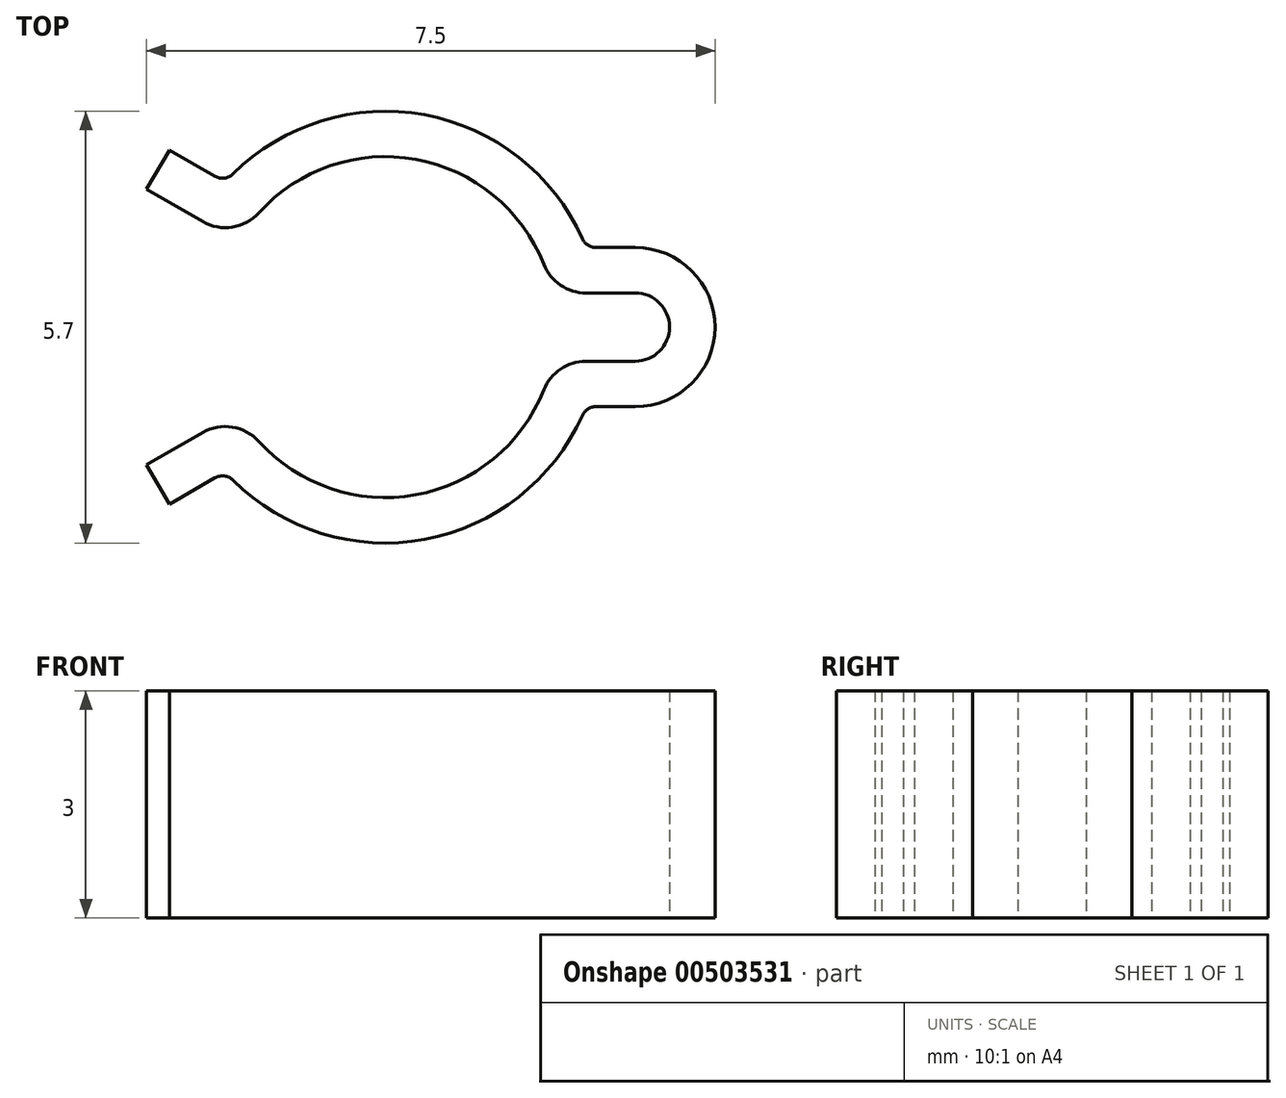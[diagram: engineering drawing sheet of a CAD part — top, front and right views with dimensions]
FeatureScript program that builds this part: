
annotation { "Feature Type Name" : "Feature", "Feature Type Description" : "" }
export const myFeature = defineFeature(function(context is Context, id is Id, definition is map)
    precondition{}
    {
        {
            var Q0;
            Q0=qCreatedBy(makeId("Top.planeOp"),FACE);
            var sketch = newSketch(context, id + "F0", { "sketchPlane" : qUnion([Q0])});
            skArc(sketch, "E0", {"start": v(0.7, 0.28) * mm, "mid": v(0.13, 0.74) * mm, "end": v(-0.56, 0.5) * mm});
            skArc(sketch, "E1", {"start": v(0.8, 0.31) * mm, "mid": v(0.15, 0.84) * mm, "end": v(-0.63, 0.57) * mm});
            skLineSegment(sketch, "E2", {"start": v(0, 0) * mm, "end": v(-1.2, 0.7) * mm, "construction": true});
            skLineSegment(sketch, "E3", {"start": v(0, 0) * mm, "end": v(-1.2, -0.7) * mm, "construction": true});
            skCircle(sketch, "E4", {"center": v(0, 0) * mm, "radius": 1.35 * mm, "construction": true});
            skArc(sketch, "E5", {"start": v(1.1, -0.25) * mm, "mid": v(1.35, 0) * mm, "end": v(1.1, 0.25) * mm});
            skArc(sketch, "E6", {"start": v(1.1, -0.15) * mm, "mid": v(1.25, 0) * mm, "end": v(1.1, 0.15) * mm});
            skLineSegment(sketch, "E7", {"start": v(1.1, 0.25) * mm, "end": v(0.88, 0.25) * mm});
            skLineSegment(sketch, "E8", {"start": v(1.1, 0.15) * mm, "end": v(0.88, 0.15) * mm});
            skLineSegment(sketch, "E9", {"start": v(1.1, -0.15) * mm, "end": v(0.88, -0.15) * mm});
            skLineSegment(sketch, "E10", {"start": v(1.1, -0.25) * mm, "end": v(0.88, -0.25) * mm});
            skPoint(sketch, "E11.visualSharp", {"position": v(0.81, 0.25) * mm});
            skArc(sketch, "E11.filletArc", {"start": v(0.8, 0.31) * mm, "mid": v(0.83, 0.27) * mm, "end": v(0.88, 0.25) * mm});
            skPoint(sketch, "E12.visualSharp", {"position": v(0.73, 0.15) * mm});
            skArc(sketch, "E12.filletArc", {"start": v(0.7, 0.28) * mm, "mid": v(0.77, 0.18) * mm, "end": v(0.88, 0.15) * mm});
            skPoint(sketch, "E13.visualSharp", {"position": v(0.81, -0.25) * mm});
            skArc(sketch, "E13.filletArc", {"start": v(0.88, -0.25) * mm, "mid": v(0.83, -0.27) * mm, "end": v(0.8, -0.31) * mm});
            skPoint(sketch, "E14.visualSharp", {"position": v(0.73, -0.15) * mm});
            skArc(sketch, "E14.filletArc", {"start": v(0.88, -0.15) * mm, "mid": v(0.77, -0.18) * mm, "end": v(0.7, -0.28) * mm});
            skLineSegment(sketch, "E15", {"start": v(1.35, 0) * mm, "end": v(-1.05, 0) * mm, "construction": true});
            skLineSegment(sketch, "E16", {"start": v(-1.05, -0.6) * mm, "end": v(-0.8, -0.46) * mm});
            skLineSegment(sketch, "E17", {"start": v(-1.05, 0.6) * mm, "end": v(-0.8, 0.46) * mm});
            skLineSegment(sketch, "E18", {"start": v(-1.05, 0.6) * mm, "end": v(-1, 0.7) * mm});
            skLineSegment(sketch, "E19", {"start": v(-1.05, -0.6) * mm, "end": v(-1, -0.7) * mm});
            skLineSegment(sketch, "E20", {"start": v(-1, -0.7) * mm, "end": v(-0.75, -0.55) * mm});
            skLineSegment(sketch, "E21", {"start": v(-1, 0.7) * mm, "end": v(-0.75, 0.55) * mm});
            skArc(sketch, "E22.trimOffspring", {"start": v(-0.56, -0.5) * mm, "mid": v(0.13, -0.74) * mm, "end": v(0.7, -0.28) * mm});
            skArc(sketch, "E23.trimOffspring", {"start": v(-0.63, -0.57) * mm, "mid": v(0.15, -0.84) * mm, "end": v(0.8, -0.31) * mm});
            skPoint(sketch, "E24.visualSharp", {"position": v(-0.68, 0.5) * mm});
            skArc(sketch, "E24.filletArc", {"start": v(-0.75, 0.55) * mm, "mid": v(-0.69, 0.54) * mm, "end": v(-0.63, 0.57) * mm});
            skPoint(sketch, "E25.visualSharp", {"position": v(-0.65, 0.38) * mm});
            skArc(sketch, "E25.filletArc", {"start": v(-0.8, 0.46) * mm, "mid": v(-0.67, 0.44) * mm, "end": v(-0.56, 0.5) * mm});
            skPoint(sketch, "E26.visualSharp", {"position": v(-0.68, -0.5) * mm});
            skArc(sketch, "E26.filletArc", {"start": v(-0.63, -0.57) * mm, "mid": v(-0.69, -0.54) * mm, "end": v(-0.75, -0.55) * mm});
            skPoint(sketch, "E27.visualSharp", {"position": v(-0.65, -0.38) * mm});
            skArc(sketch, "E27.filletArc", {"start": v(-0.56, -0.5) * mm, "mid": v(-0.67, -0.44) * mm, "end": v(-0.8, -0.46) * mm});
            skLineSegment(sketch, "E28.0", {"start": v(-0.95, -0.78) * mm, "end": v(-0.7, -0.64) * mm});
            skArc(sketch, "E28.1", {"start": v(-0.7, -0.64) * mm, "mid": v(0.17, -0.93) * mm, "end": v(0.88, -0.35) * mm});
            skLineSegment(sketch, "E28.2", {"start": v(1.1, -0.35) * mm, "end": v(0.88, -0.35) * mm});
            skLineSegment(sketch, "E28.3", {"start": v(-0.95, 0.78) * mm, "end": v(-0.7, 0.64) * mm});
            skArc(sketch, "E28.4", {"start": v(0.88, 0.35) * mm, "mid": v(0.17, 0.93) * mm, "end": v(-0.7, 0.64) * mm});
            skLineSegment(sketch, "E28.5", {"start": v(1.1, 0.35) * mm, "end": v(0.88, 0.35) * mm});
            skArc(sketch, "E28.6", {"start": v(1.1, -0.35) * mm, "mid": v(1.45, 0) * mm, "end": v(1.1, 0.35) * mm});
            skLineSegment(sketch, "E29", {"start": v(-0.95, 0.78) * mm, "end": v(-1, 0.7) * mm});
            skLineSegment(sketch, "E30", {"start": v(-1, -0.7) * mm, "end": v(-0.95, -0.78) * mm});
            skSolve(sketch);
        }
        {
            var Q0;
            Q0=makeQuery(id+"F0.imprint","IMPRINT",FACE,{"disambiguationData":[TD([[makeQuery(id+"F0.imprint","IMPRINT",EDGE,{"derivedFrom":sQuery(id+"F0.wireOp",EDGE,"E0")}),-1.0]])]});
            var Q1;
            Q1=makeQuery(id+"F0.imprint","IMPRINT",FACE,{"disambiguationData":[TD([[makeQuery(id+"F0.imprint","IMPRINT",EDGE,{"derivedFrom":sQuery(id+"F0.wireOp",EDGE,"E1")}),-1.0]])]});
            extrude(context, id + "F1", {"entities" : qUnion([Q0, Q1]), "depth" : 1 * mm});
        }
        {
            var Q0;
            Q0=makeQuery(id+"F1.opExtrude","SWEPT_BODY",BODY,{"disambiguationData":[OSD([sQuery(id+"F0.wireOp",EDGE,"E0"),sQuery(id+"F0.wireOp",EDGE,"E1"),sQuery(id+"F0.wireOp",EDGE,"E5"),sQuery(id+"F0.wireOp",EDGE,"E6"),sQuery(id+"F0.wireOp",EDGE,"E7"),sQuery(id+"F0.wireOp",EDGE,"E8"),sQuery(id+"F0.wireOp",EDGE,"E9"),sQuery(id+"F0.wireOp",EDGE,"E10"),sQuery(id+"F0.wireOp",EDGE,"E11.filletArc"),sQuery(id+"F0.wireOp",EDGE,"E12.filletArc"),sQuery(id+"F0.wireOp",EDGE,"E13.filletArc"),sQuery(id+"F0.wireOp",EDGE,"E14.filletArc"),sQuery(id+"F0.wireOp",EDGE,"E16"),sQuery(id+"F0.wireOp",EDGE,"E17"),sQuery(id+"F0.wireOp",EDGE,"E18"),sQuery(id+"F0.wireOp",EDGE,"E19"),sQuery(id+"F0.wireOp",EDGE,"E20"),sQuery(id+"F0.wireOp",EDGE,"E21"),sQuery(id+"F0.wireOp",EDGE,"E22.trimOffspring"),sQuery(id+"F0.wireOp",EDGE,"E23.trimOffspring"),sQuery(id+"F0.wireOp",EDGE,"E24.filletArc"),sQuery(id+"F0.wireOp",EDGE,"E25.filletArc"),sQuery(id+"F0.wireOp",EDGE,"E26.filletArc"),sQuery(id+"F0.wireOp",EDGE,"E27.filletArc")])]});
            var Q1;
            Q1=qCreatedBy(makeId("Origin.pointOp"),VERTEX);
            transform(context, id + "F2", {"entities" : qUnion([Q0]), "transformType" : TransformType.SCALE_UNIFORMLY, "scale" : 3, "makeCopy" : false, "scalePoint" : qUnion([Q1])});
        }
        {
            var Q0;
            Q0=makeQuery(id+"F1.opExtrude","SWEPT_EDGE",EDGE,{"disambiguationData":[OSD([sQuery(id+"F0.wireOp",EDGE,"E28.3"),sQuery(id+"F0.wireOp",EDGE,"E28.4")])]});
            var Q1;
            Q1=makeQuery(id+"F1.opExtrude","SWEPT_EDGE",EDGE,{"disambiguationData":[OSD([sQuery(id+"F0.wireOp",EDGE,"E28.0"),sQuery(id+"F0.wireOp",EDGE,"E28.1")])]});
            var Q2;
            Q2=makeQuery(id+"F1.opExtrude","SWEPT_EDGE",EDGE,{"disambiguationData":[OSD([sQuery(id+"F0.wireOp",EDGE,"E28.1"),sQuery(id+"F0.wireOp",EDGE,"E28.2")])]});
            var Q3;
            Q3=makeQuery(id+"F1.opExtrude","SWEPT_EDGE",EDGE,{"disambiguationData":[OSD([sQuery(id+"F0.wireOp",EDGE,"E28.4"),sQuery(id+"F0.wireOp",EDGE,"E28.5")])]});
            fillet(context, id + "F3", {"entities" : qUnion([Q0, Q1, Q2, Q3]), "radius" : 0.2 * mm, "tangentPropagation" : true, "allowEdgeOverflow" : false});
        }
    });
